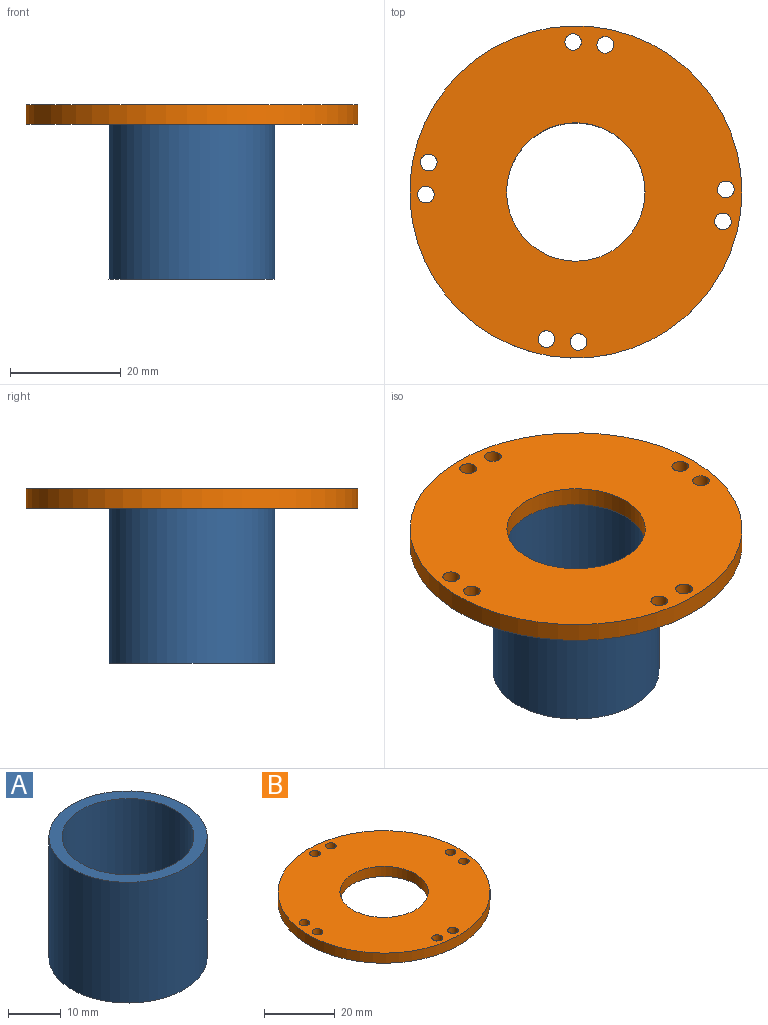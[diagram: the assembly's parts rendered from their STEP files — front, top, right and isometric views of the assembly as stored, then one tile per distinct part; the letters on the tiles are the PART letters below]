
ASSEMBLY  parts=2 mates=1
PART A: 4 faces, bbox 30x30x28 mm
  f0: cylinder r=12.5mm len=28mm, axis (0,0,-1), area 2199.1mm2, adj f2,f3
  f1: cylinder r=15mm len=30mm, axis (0,0,-1), area 2638.9mm2, adj f2,f3
  f2: plane 30x30mm, normal (0,0,1), area 216mm2, adj f0,f1
  f3: plane 30x30mm, normal (0,0,-1), area 216mm2, adj f0,f1
PART B: 12 faces, bbox 60x60x3.5 mm
  f0: cylinder r=1.5mm len=3.5mm, axis (0,0,1), area 33mm2, adj f8,f9
  f1: cylinder r=1.5mm len=3.5mm, axis (0,0,1), area 33mm2, adj f8,f9
  f2: cylinder r=1.5mm len=3.5mm, axis (0,0,1), area 33mm2, adj f8,f9
  f3: cylinder r=1.5mm len=3.5mm, axis (0,0,1), area 33mm2, adj f8,f9
  f4: cylinder r=1.5mm len=3.5mm, axis (0,0,1), area 33mm2, adj f8,f9
  f5: cylinder r=1.5mm len=3.5mm, axis (0,0,1), area 33mm2, adj f8,f9
  f6: cylinder r=12.5mm len=25mm, axis (0,0,-1), area 274.9mm2, adj f8,f9
  f7: cylinder r=30mm len=60mm, axis (0,0,-1), area 659.7mm2, adj f8,f9
  f8: plane 60x60mm, normal (0,0,1), area 2280mm2, adj f0,f1,f2,f3,f4,f5,f6,f7
  f9: plane 60x60mm, normal (0,0,-1), area 2280mm2, adj f0,f1,f2,f3,f4,f5,f6,f7
  f10: cylinder r=1.5mm len=3.5mm, axis (0,0,1), area 33mm2, adj f8,f9
  f11: cylinder r=1.5mm len=3.5mm, axis (0,0,1), area 33mm2, adj f8,f9
PLACE A t=(-49.25,-0.07,27.92)mm
PLACE B t=(16.13,2.24,55.92)mm
MATE fastened B.f6 <-> A.f0  axis (0,0,-1) through (-7.23,23.77,55.92)mm
